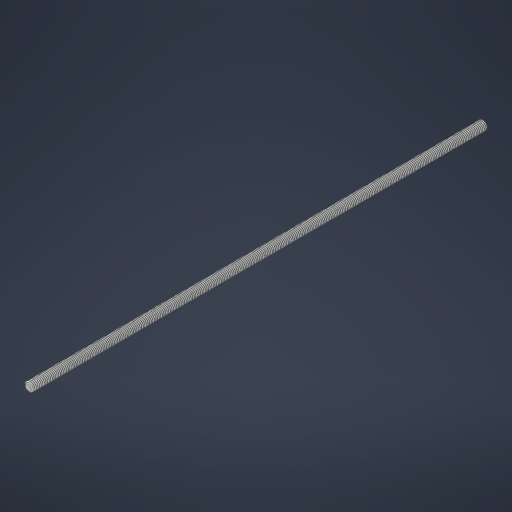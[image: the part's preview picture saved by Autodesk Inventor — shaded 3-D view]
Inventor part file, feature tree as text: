
AUTODESK INVENTOR PART (.ipt)
format: ipt  version: 2023 (Build 270158000, 158)  size: 4,833,792 bytes
history: native  units: in
note: dims shown in document units (in); Inventor stores cm internally (conversion verified against a paired STEP export)
features: mirror x1
ambient origin geometry x8: Origin, YZ Plane, XZ Plane, XY Plane, X Axis, Y Axis, Z Axis, Center Point
bodies: Solid1 (feature_tree)
feature tree (1):
  mirror  "Mirror1"
